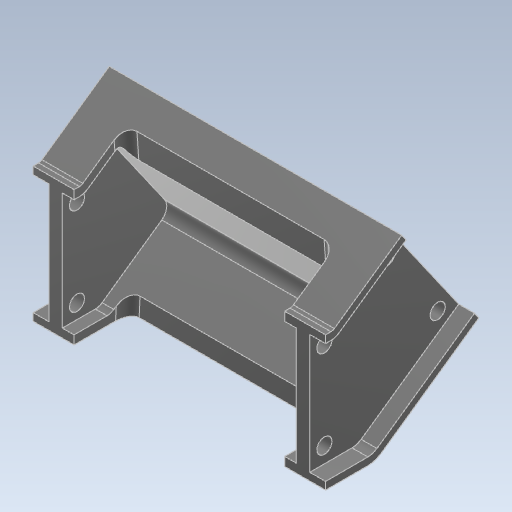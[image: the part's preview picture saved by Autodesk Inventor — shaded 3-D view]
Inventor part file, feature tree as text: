
AUTODESK INVENTOR PART (.ipt)
format: ipt  version: 2024 (Build 280153000, 153)  size: 307,712 bytes
history: native  units: mm
features: other x10, chamfer x2, fillet x1
ambient origin geometry x8: Origin, YZ Plane, XZ Plane, XY Plane, X Axis, Y Axis, Z Axis, Center Point
bodies: Body1 (feature_tree)
feature tree (13):
  other  "_bridseye_sketch.ipt"
  chamfer  "面取り1"  Distance=10.0mm
  chamfer  "面取り2"  Distance=10.0mm Angle=45.0deg
  fillet  "フィレット1"  Radius=10.0mm
  other  "厚み1"
  other  "厚み2"
  other  "厚み3"
  other  "厚み4"
  other  "厚み5"
  other  "厚み6"
  other  "ソリッド15::_bridseye_sketch.ipt"
  other  "TaggingFeature1"
  other  "side_links-link1_link1Conn"
